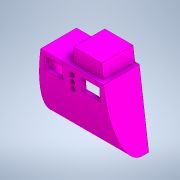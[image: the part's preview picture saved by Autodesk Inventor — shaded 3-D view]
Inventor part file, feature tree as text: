
AUTODESK INVENTOR PART (.ipt)
format: ipt  version: 2020 (Build 240168000, 168)  size: 325,120 bytes
history: native  units: mm
features: sketch x9, extrude x9, other x5, plane x4, reference x4, projected_geometry x4
ambient origin geometry x8: Origin, YZ Plane, XZ Plane, XY Plane, X Axis, Y Axis, Z Axis, Center Point
bodies: Solid1 (feature_tree)
feature tree (35):
  sketch  "Sketch1"  dims[d0=10.0mm d1=0.0mm d2=1.0mm d3=0.0mm]
  plane  "Work Plane1"
  extrude  "Extrusion1"  Depth=1.0mm TaperAngle=0.0deg
  extrude  "Extrusion2"  Depth=70.0mm
  sketch  "Sketch3"  dims[d7=0.0mm d8=0.0mm d9=5.0mm]
  plane  "Work Plane2"
  extrude  "Extrusion3"  Depth=5.0mm
  plane  "Work Plane3"
  extrude  "Extrusion4"  Depth=10.0mm TaperAngle=0.0deg
  sketch  "Sketch7"  dims[d16=4.0mm d17=0.0mm d18=0.0mm]
  other  "Work Point1"
  extrude  "Extrusion5"  TaperAngle=0.0deg  [1 undecoded]
  extrude  "Extrusion6"  Depth=19.8mm
  extrude  "Extrusion7"  Depth=19.8mm
  plane  "Work Plane4"
  extrude  "Extrusion8"  Depth=5.0mm
  extrude  "Extrusion9"  Depth=3.0mm
  reference  "Reference1"
  sketch  "Sketch2"  dims[d4=1.0mm d5=0.0mm d6=70.0mm]
  reference  "Reference2"
  projected_geometry  "Projected Loop1"
  projected_geometry  "Projected Loop2"
  sketch  "Sketch4"  dims[d10=5.0mm d11=10.0mm d12=0.0mm]
  reference  "Reference3"
  projected_geometry  "Projected Loop3"
  reference  "Reference4"
  sketch  "Sketch14"  dims[d19=0.0mm d20=0.0mm d21=19.8mm]
  sketch  "Sketch15"  dims[d22=13.8mm d23=19.8mm]
  projected_geometry  "Projected Loop5"
  sketch  "Sketch16"  dims[d24=13.8mm d25=5.0mm]
  sketch  "Sketch17"  dims[d27=30.0mm d29=7.0mm d30=10.0mm d32=10.0mm d34=3.0mm d35=10.0mm d36=0.0mm d37=3.0mm d38=0.0mm]
  parser-record x1  (decoder bookkeeping rows leaked as tree rows — omitted from the tree; the rows remain in map.json)
  other  "steering_queens_pair.iam"
  other  "hull_electronics:1"
  other  "hull_main:1"
note: 1 required parameter value undecoded (feature->parameter linkage not recoverable at this tier; creation-order binding heuristic only, values carry confidence <= 0.55)
note: 1 file-system path scrubbed to <path> (originals preserved in map.json)
